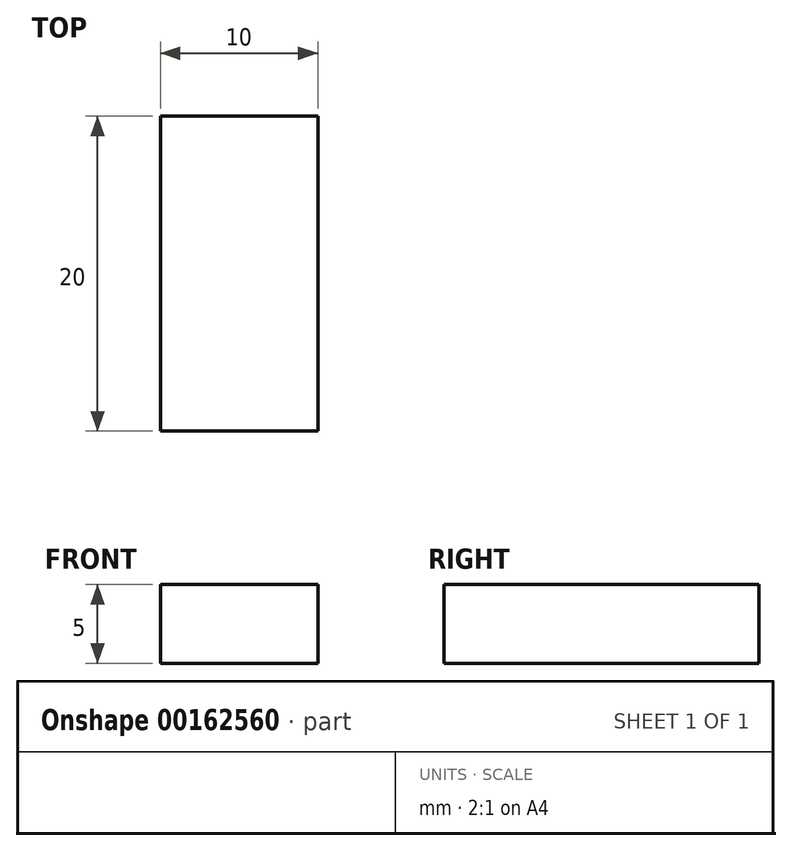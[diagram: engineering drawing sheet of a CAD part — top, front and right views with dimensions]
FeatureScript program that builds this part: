
annotation { "Feature Type Name" : "Feature", "Feature Type Description" : "" }
export const myFeature = defineFeature(function(context is Context, id is Id, definition is map)
    precondition{}
    {
        {
            var Q0;
            Q0=qCreatedBy(makeId("Top.planeOp"),FACE);
            var sketch = newSketch(context, id + "F0", { "sketchPlane" : qUnion([Q0])});
            skLineSegment(sketch, "E0.bottom", {"start": v(-5, 10) * mm, "end": v(5, 10) * mm});
            skLineSegment(sketch, "E0.top", {"start": v(-5, -10) * mm, "end": v(5, -10) * mm});
            skLineSegment(sketch, "E0.left", {"start": v(-5, 10) * mm, "end": v(-5, -10) * mm});
            skLineSegment(sketch, "E0.right", {"start": v(5, 10) * mm, "end": v(5, -10) * mm});
            skSolve(sketch);
        }
        {
            var Q0;
            Q0 = qSketchRegion(id + "F0", true);
            extrude(context, id + "F1", {"entities" : qUnion([Q0]), "depth" : 5 * mm});
        }
    });
